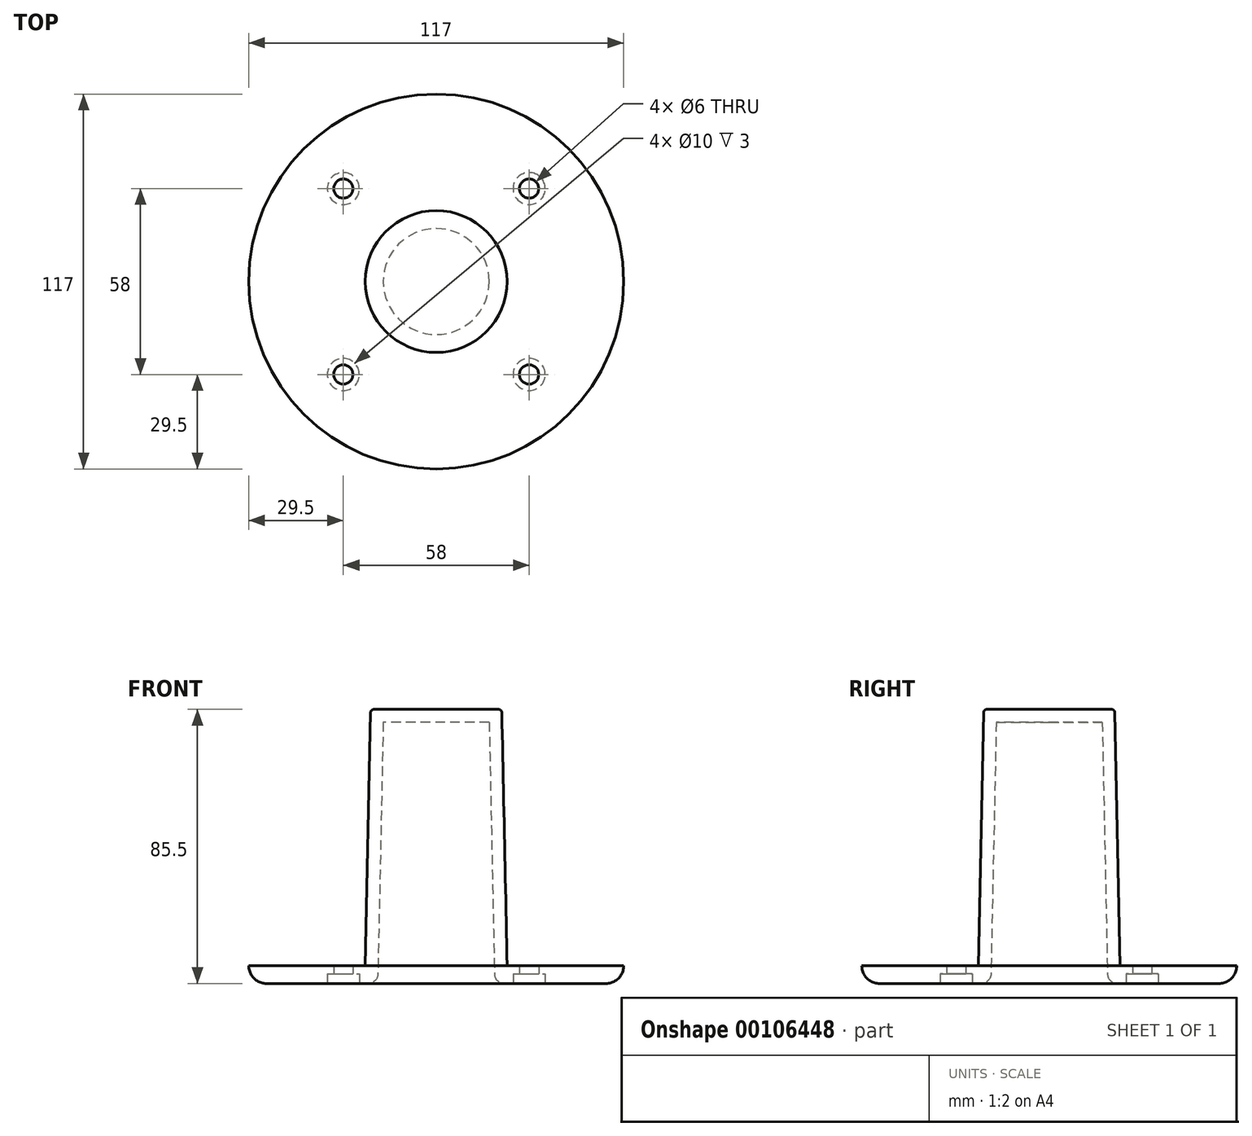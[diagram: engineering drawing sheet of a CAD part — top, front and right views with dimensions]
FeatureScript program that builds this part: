
annotation { "Feature Type Name" : "Feature", "Feature Type Description" : "" }
export const myFeature = defineFeature(function(context is Context, id is Id, definition is map)
    precondition{}
    {
        {
            var Q0;
            Q0=qCreatedBy(makeId("Top.planeOp"),FACE);
            var sketch = newSketch(context, id + "F0", { "sketchPlane" : qUnion([Q0])});
            skCircle(sketch, "E0", {"center": v(0, 0) * mm, "radius": 58.5 * mm});
            skCircle(sketch, "E1", {"center": v(0, 0) * mm, "radius": 22.25 * mm});
            skLineSegment(sketch, "E2.bottom", {"start": v(29, 29) * mm, "end": v(-29, 29) * mm, "construction": true});
            skLineSegment(sketch, "E2.top", {"start": v(29, -29) * mm, "end": v(-29, -29) * mm, "construction": true});
            skLineSegment(sketch, "E2.left", {"start": v(29, 29) * mm, "end": v(29, -29) * mm, "construction": true});
            skLineSegment(sketch, "E2.right", {"start": v(-29, 29) * mm, "end": v(-29, -29) * mm, "construction": true});
            skCircle(sketch, "E3", {"center": v(-29, 29) * mm, "radius": 3 * mm});
            skCircle(sketch, "E4", {"center": v(-29, -29) * mm, "radius": 3 * mm});
            skCircle(sketch, "E5", {"center": v(29, 29) * mm, "radius": 3 * mm});
            skCircle(sketch, "E6", {"center": v(29, -29) * mm, "radius": 3 * mm});
            skCircle(sketch, "E7.0", {"center": v(0, 0) * mm, "radius": 21.25 * mm});
            skSolve(sketch);
        }
        {
            var Q0;
            Q0=makeQuery(id+"F0.imprint","IMPRINT",FACE,{"disambiguationData":[TD([[makeQuery(id+"F0.imprint","IMPRINT",EDGE,{"derivedFrom":sQuery(id+"F0.wireOp",EDGE,"E7.0")}),1.0]])]});
            var Q1;
            Q1=makeQuery(id+"F0.imprint","IMPRINT",FACE,{"disambiguationData":[TD([[makeQuery(id+"F0.imprint","IMPRINT",EDGE,{"derivedFrom":sQuery(id+"F0.wireOp",EDGE,"E1")}),1.0]])]});
            extrude(context, id + "F1", {"entities" : qUnion([Q0, Q1]), "depth" : 85.5 * mm, "offsetDistance" : 25 * mm, "hasDraft" : true, "draftAngle" : 1.2 * degree, "draftPullDirection" : true});
        }
        {
            var Q0;
            Q0=makeQuery(id+"F1.opExtrude","CAP_FACE",FACE,{"disambiguationData":[OSD([sQuery(id+"F0.wireOp",EDGE,"E1")])],"isStart":true});
            shell(context, id + "F2", {"entities" : qUnion([Q0]), "thickness" : 4 * mm});
        }
        {
            var Q0;
            Q0=makeQuery(id+"F0.imprint","IMPRINT",FACE,{"disambiguationData":[TD([[makeQuery(id+"F0.imprint","IMPRINT",EDGE,{"derivedFrom":sQuery(id+"F0.wireOp",EDGE,"E0")}),1.0]])]});
            var Q1;
            Q1=makeQuery(id+"F0.imprint","IMPRINT",FACE,{"disambiguationData":[TD([[makeQuery(id+"F0.imprint","IMPRINT",EDGE,{"derivedFrom":sQuery(id+"F0.wireOp",EDGE,"E1")}),1.0]])]});
            extrude(context, id + "F3", {"entities" : qUnion([Q0, Q1]), "operationType" : NewBodyOperationType.ADD, "depth" : 5.5 * mm, "offsetDistance" : 25 * mm});
        }
        {
            var Q0;
            Q0=makeQuery(id+"F3.opExtrude","CAP_EDGE",EDGE,{"disambiguationData":[OSD([sQuery(id+"F0.wireOp",EDGE,"E0")])],"isStart":true});
            fillet(context, id + "F4", {"entities" : qUnion([Q0]), "tangentPropagation" : true, "radius" : 5.5 * mm, "defaultsChanged" : true, "vertexSettings" : [], "allowEdgeOverflow" : false});
        }
        {
            var Q0;
            Q0=sQuery(id+"F0.wireOp",VERTEX,"E2.bottom.start");
            var Q1;
            Q1=sQuery(id+"F0.wireOp",VERTEX,"E2.bottom.end");
            var Q2;
            Q2=sQuery(id+"F0.wireOp",VERTEX,"E2.top.end");
            var Q3;
            Q3=sQuery(id+"F0.wireOp",VERTEX,"E2.top.start");
            var Q4;
            Q4=makeQuery(id+"F1.opExtrude","SWEPT_BODY",BODY,{"disambiguationData":[OSD([sQuery(id+"F0.wireOp",EDGE,"E1")])]});
            hole(context, id + "F5", {"style" : HoleStyle.C_BORE, "endStyle" : HoleEndStyle.BLIND, "oppositeDirection" : true, "holeDiameter" : 6 * mm, "cBoreDiameter" : 10 * mm, "cBoreDepth" : 3 * mm, "majorDiameter" : 5 * mm, "holeDepth" : 5 * mm, "isTappedThrough" : true, "tappedDepth" : 12 * mm, "tapClearance" : 3, "locations" : qUnion([Q0, Q1, Q2, Q3]), "scope" : qUnion([Q4])});
        }
        {
            var Q0;
            Q0=makeQuery(id+"F1.opExtrude","CAP_EDGE",EDGE,{"disambiguationData":[OSD([sQuery(id+"F0.wireOp",EDGE,"E1")])],"isStart":false});
            fillet(context, id + "F6", {"entities" : qUnion([Q0]), "tangentPropagation" : true, "radius" : 1 * mm, "defaultsChanged" : true, "vertexSettings" : [], "allowEdgeOverflow" : false});
        }
        {
            var Q0;
            {var subQ0=sQuery(id+"F0.wireOp",EDGE,"E1");Q0=makeQuery(id+"F2.opShell","OFFSET_EDGE",EDGE,{"disambiguationData":[OSD([subQ0]),TDD([makeQuery(id+"F1.opExtrude","CAP_EDGE",EDGE,{"disambiguationData":[OSD([subQ0])],"isStart":true})])]});}
            fillet(context, id + "F7", {"entities" : qUnion([Q0]), "tangentPropagation" : true, "radius" : 3 * mm, "defaultsChanged" : true, "vertexSettings" : [], "allowEdgeOverflow" : false});
        }
    });
